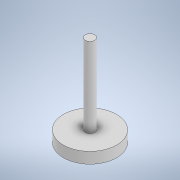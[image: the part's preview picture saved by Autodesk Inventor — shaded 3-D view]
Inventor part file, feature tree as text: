
AUTODESK INVENTOR PART (.ipt)
format: ipt  version: 2021 (Build 250183000, 183)  size: 102,400 bytes
history: native  units: in
note: dims shown in document units (in); Inventor stores cm internally (conversion verified against a paired STEP export)
features: revolve x1, sketch x1
ambient origin geometry x8: Origin, YZ Plane, XZ Plane, XY Plane, X Axis, Y Axis, Z Axis, Center Point
bodies: Solid1 (feature_tree)
feature tree (2):
  revolve  "Revolution1"  [1 undecoded]
  sketch  "Sketch2"  dims[d0=0.4724in d1=0.0846in d2=0.1969in d3=1.4173in d4=90.0deg]
note: 1 required parameter value undecoded (feature->parameter linkage not recoverable at this tier; creation-order binding heuristic only, values carry confidence <= 0.55)
